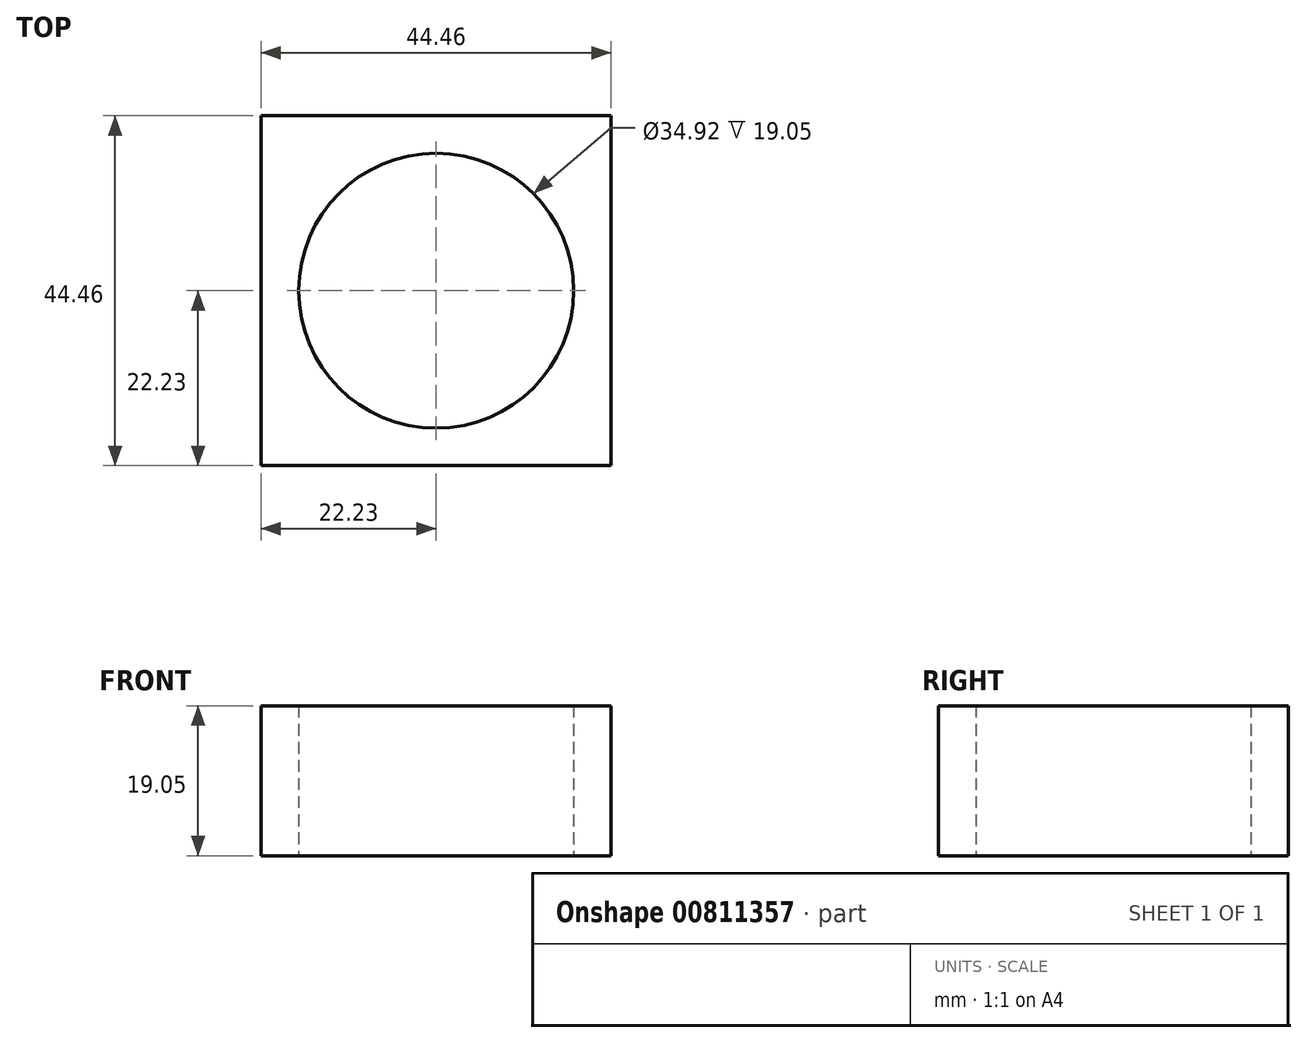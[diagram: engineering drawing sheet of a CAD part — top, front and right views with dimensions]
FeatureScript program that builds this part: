
annotation { "Feature Type Name" : "Feature", "Feature Type Description" : "" }
export const myFeature = defineFeature(function(context is Context, id is Id, definition is map)
    precondition{}
    {
        {
            var Q0;
            Q0=qCreatedBy(makeId("Top.planeOp"),FACE);
            var sketch = newSketch(context, id + "F0", { "sketchPlane" : qUnion([Q0])});
            skLineSegment(sketch, "E0.bottom", {"start": v(-22.22, 22.22) * mm, "end": v(22.23, 22.22) * mm});
            skLineSegment(sketch, "E0.top", {"start": v(-22.23, -22.23) * mm, "end": v(22.22, -22.23) * mm});
            skLineSegment(sketch, "E0.left", {"start": v(-22.22, 22.22) * mm, "end": v(-22.23, -22.23) * mm});
            skLineSegment(sketch, "E0.right", {"start": v(22.23, 22.22) * mm, "end": v(22.22, -22.23) * mm});
            skPoint(sketch, "E0.middle", {"position": v(0, 0) * mm});
            skCircle(sketch, "E1", {"center": v(0, 0) * mm, "radius": 17.46 * mm});
            skSolve(sketch);
        }
        {
            var Q0;
            Q0=makeQuery(id+"F0.imprint","IMPRINT",FACE,{"disambiguationData":[TD([[makeQuery(id+"F0.imprint","IMPRINT",EDGE,{"derivedFrom":sQuery(id+"F0.wireOp",EDGE,"E0.bottom")}),-1.0]])]});
            extrude(context, id + "F1", {"entities" : qUnion([Q0]), "depth" : 19.05 * mm, "offsetDistance" : 25.4 * mm});
        }
    });
